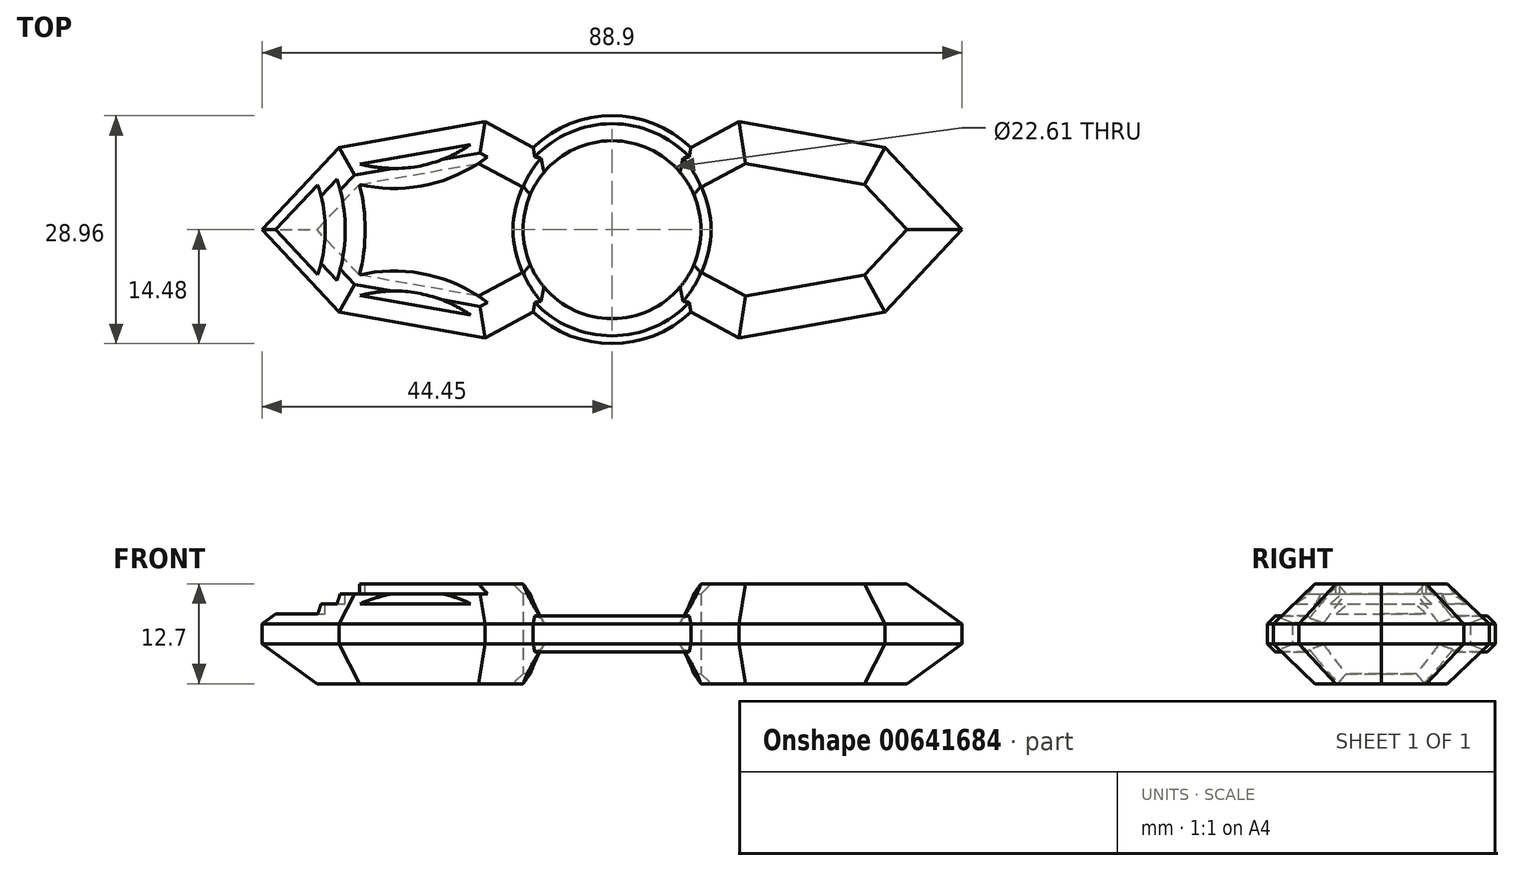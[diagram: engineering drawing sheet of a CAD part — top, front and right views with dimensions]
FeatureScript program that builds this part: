
annotation { "Feature Type Name" : "Feature", "Feature Type Description" : "" }
export const myFeature = defineFeature(function(context is Context, id is Id, definition is map)
    precondition{}
    {
        {
            var Q0;
            Q0=qCreatedBy(makeId("Top.planeOp"),FACE);
            var sketch = newSketch(context, id + "F0", { "sketchPlane" : qUnion([Q0])});
            skCircle(sketch, "E0", {"center": v(0, 0) * mm, "radius": 11.3 * mm});
            skArc(sketch, "E1", {"start": v(-10, -10.47) * mm, "mid": v(0, -14.48) * mm, "end": v(10, -10.47) * mm});
            skLineSegment(sketch, "E2", {"start": v(-10, 10.47) * mm, "end": v(-16.15, 13.73) * mm});
            skLineSegment(sketch, "E3", {"start": v(-34.65, 10.47) * mm, "end": v(-16.15, 13.73) * mm});
            skLineSegment(sketch, "E4", {"start": v(-44.45, 0) * mm, "end": v(-34.65, 10.47) * mm});
            skLineSegment(sketch, "E5", {"start": v(-44.45, 0) * mm, "end": v(44.45, 0) * mm, "construction": true});
            skLineSegment(sketch, "E6", {"start": v(0, 64.66) * mm, "end": v(0, -71.54) * mm, "construction": true});
            skArc(sketch, "E7.trimOffspring", {"start": v(10, 10.47) * mm, "mid": v(0, 14.48) * mm, "end": v(-10, 10.47) * mm});
            skLineSegment(sketch, "E8.MirrorCS", {"start": v(-44.45, 0) * mm, "end": v(-34.65, -10.47) * mm});
            skLineSegment(sketch, "E9.MirrorCS", {"start": v(-34.65, -10.47) * mm, "end": v(-16.15, -13.73) * mm});
            skLineSegment(sketch, "E10.MirrorCS", {"start": v(-10, -10.47) * mm, "end": v(-16.15, -13.73) * mm});
            skLineSegment(sketch, "E11.MirrorCS", {"start": v(10, 10.47) * mm, "end": v(16.15, 13.73) * mm});
            skLineSegment(sketch, "E12.MirrorCS", {"start": v(34.65, 10.47) * mm, "end": v(16.15, 13.73) * mm});
            skLineSegment(sketch, "E13.MirrorCS", {"start": v(44.45, 0) * mm, "end": v(34.65, 10.47) * mm});
            skLineSegment(sketch, "E14.MirrorCS", {"start": v(44.45, 0) * mm, "end": v(34.65, -10.47) * mm});
            skLineSegment(sketch, "E15.MirrorCS", {"start": v(34.65, -10.47) * mm, "end": v(16.15, -13.73) * mm});
            skLineSegment(sketch, "E16.MirrorCS", {"start": v(10, -10.47) * mm, "end": v(16.15, -13.73) * mm});
            skSolve(sketch);
        }
        {
            var Q0;
            Q0 = qSketchRegion(id + "F0", true);
            extrude(context, id + "F1", {"entities" : qUnion([Q0]), "endBound" : BoundingType.SYMMETRIC, "depth" : 12.7 * mm, "offsetDistance" : 25.4 * mm});
        }
        {
            var Q0;
            Q0=makeQuery(id+"F1.opExtrude","CAP_EDGE",EDGE,{"disambiguationData":[OSD([sQuery(id+"F0.wireOp",EDGE,"E8.MirrorCS")])],"isStart":false});
            var Q1;
            Q1=makeQuery(id+"F1.opExtrude","CAP_EDGE",EDGE,{"disambiguationData":[OSD([sQuery(id+"F0.wireOp",EDGE,"E4")])],"isStart":false});
            var Q2;
            Q2=makeQuery(id+"F1.opExtrude","CAP_EDGE",EDGE,{"disambiguationData":[OSD([sQuery(id+"F0.wireOp",EDGE,"E3")])],"isStart":false});
            var Q3;
            Q3=makeQuery(id+"F1.opExtrude","CAP_EDGE",EDGE,{"disambiguationData":[OSD([sQuery(id+"F0.wireOp",EDGE,"E2")])],"isStart":false});
            var Q4;
            Q4=makeQuery(id+"F1.opExtrude","CAP_EDGE",EDGE,{"disambiguationData":[OSD([sQuery(id+"F0.wireOp",EDGE,"E7.trimOffspring")])],"isStart":false});
            var Q5;
            Q5=makeQuery(id+"F1.opExtrude","CAP_EDGE",EDGE,{"disambiguationData":[OSD([sQuery(id+"F0.wireOp",EDGE,"E1")])],"isStart":false});
            var Q6;
            Q6=makeQuery(id+"F1.opExtrude","CAP_EDGE",EDGE,{"disambiguationData":[OSD([sQuery(id+"F0.wireOp",EDGE,"E10.MirrorCS")])],"isStart":false});
            var Q7;
            Q7=makeQuery(id+"F1.opExtrude","CAP_EDGE",EDGE,{"disambiguationData":[OSD([sQuery(id+"F0.wireOp",EDGE,"E9.MirrorCS")])],"isStart":false});
            var Q8;
            Q8=makeQuery(id+"F1.opExtrude","CAP_EDGE",EDGE,{"disambiguationData":[OSD([sQuery(id+"F0.wireOp",EDGE,"E15.MirrorCS")])],"isStart":false});
            var Q9;
            Q9=makeQuery(id+"F1.opExtrude","CAP_EDGE",EDGE,{"disambiguationData":[OSD([sQuery(id+"F0.wireOp",EDGE,"E16.MirrorCS")])],"isStart":false});
            var Q10;
            Q10=makeQuery(id+"F1.opExtrude","CAP_EDGE",EDGE,{"disambiguationData":[OSD([sQuery(id+"F0.wireOp",EDGE,"E14.MirrorCS")])],"isStart":false});
            var Q11;
            Q11=makeQuery(id+"F1.opExtrude","CAP_EDGE",EDGE,{"disambiguationData":[OSD([sQuery(id+"F0.wireOp",EDGE,"E13.MirrorCS")])],"isStart":false});
            var Q12;
            Q12=makeQuery(id+"F1.opExtrude","CAP_EDGE",EDGE,{"disambiguationData":[OSD([sQuery(id+"F0.wireOp",EDGE,"E12.MirrorCS")])],"isStart":false});
            var Q13;
            Q13=makeQuery(id+"F1.opExtrude","CAP_EDGE",EDGE,{"disambiguationData":[OSD([sQuery(id+"F0.wireOp",EDGE,"E11.MirrorCS")])],"isStart":false});
            var Q14;
            Q14=makeQuery(id+"F1.opExtrude","CAP_EDGE",EDGE,{"disambiguationData":[OSD([sQuery(id+"F0.wireOp",EDGE,"E15.MirrorCS")])],"isStart":true});
            var Q15;
            Q15=makeQuery(id+"F1.opExtrude","CAP_EDGE",EDGE,{"disambiguationData":[OSD([sQuery(id+"F0.wireOp",EDGE,"E14.MirrorCS")])],"isStart":true});
            var Q16;
            Q16=makeQuery(id+"F1.opExtrude","CAP_EDGE",EDGE,{"disambiguationData":[OSD([sQuery(id+"F0.wireOp",EDGE,"E13.MirrorCS")])],"isStart":true});
            var Q17;
            Q17=makeQuery(id+"F1.opExtrude","CAP_EDGE",EDGE,{"disambiguationData":[OSD([sQuery(id+"F0.wireOp",EDGE,"E12.MirrorCS")])],"isStart":true});
            var Q18;
            Q18=makeQuery(id+"F1.opExtrude","CAP_EDGE",EDGE,{"disambiguationData":[OSD([sQuery(id+"F0.wireOp",EDGE,"E11.MirrorCS")])],"isStart":true});
            var Q19;
            Q19=makeQuery(id+"F1.opExtrude","CAP_EDGE",EDGE,{"disambiguationData":[OSD([sQuery(id+"F0.wireOp",EDGE,"E7.trimOffspring")])],"isStart":true});
            var Q20;
            Q20=makeQuery(id+"F1.opExtrude","CAP_EDGE",EDGE,{"disambiguationData":[OSD([sQuery(id+"F0.wireOp",EDGE,"E2")])],"isStart":true});
            var Q21;
            Q21=makeQuery(id+"F1.opExtrude","CAP_EDGE",EDGE,{"disambiguationData":[OSD([sQuery(id+"F0.wireOp",EDGE,"E3")])],"isStart":true});
            var Q22;
            Q22=makeQuery(id+"F1.opExtrude","CAP_EDGE",EDGE,{"disambiguationData":[OSD([sQuery(id+"F0.wireOp",EDGE,"E4")])],"isStart":true});
            var Q23;
            Q23=makeQuery(id+"F1.opExtrude","CAP_EDGE",EDGE,{"disambiguationData":[OSD([sQuery(id+"F0.wireOp",EDGE,"E8.MirrorCS")])],"isStart":true});
            var Q24;
            Q24=makeQuery(id+"F1.opExtrude","CAP_EDGE",EDGE,{"disambiguationData":[OSD([sQuery(id+"F0.wireOp",EDGE,"E9.MirrorCS")])],"isStart":true});
            var Q25;
            Q25=makeQuery(id+"F1.opExtrude","CAP_EDGE",EDGE,{"disambiguationData":[OSD([sQuery(id+"F0.wireOp",EDGE,"E10.MirrorCS")])],"isStart":true});
            var Q26;
            Q26=makeQuery(id+"F1.opExtrude","CAP_EDGE",EDGE,{"disambiguationData":[OSD([sQuery(id+"F0.wireOp",EDGE,"E1")])],"isStart":true});
            var Q27;
            Q27=makeQuery(id+"F1.opExtrude","CAP_EDGE",EDGE,{"disambiguationData":[OSD([sQuery(id+"F0.wireOp",EDGE,"E16.MirrorCS")])],"isStart":true});
            chamfer(context, id + "F2", {"entities" : qUnion([Q0, Q1, Q2, Q3, Q4, Q5, Q6, Q7, Q8, Q9, Q10, Q11, Q12, Q13, Q14, Q15, Q16, Q17, Q18, Q19, Q20, Q21, Q22, Q23, Q24, Q25, Q26, Q27]), "width" : 5.08 * mm, "tangentPropagation" : true});
        }
        {
            var Q0;
            Q0=makeQuery(id+"F2.opChamfer","SPLIT",FACE,{"disambiguationData":[OD(0.0)],"derivedFrom":makeQuery(id+"F1.opExtrude","CAP_FACE",FACE,{"disambiguationData":[OSD([sQuery(id+"F0.wireOp",EDGE,"E0"),sQuery(id+"F0.wireOp",EDGE,"E1"),sQuery(id+"F0.wireOp",EDGE,"E2"),sQuery(id+"F0.wireOp",EDGE,"E3"),sQuery(id+"F0.wireOp",EDGE,"E4"),sQuery(id+"F0.wireOp",EDGE,"E7.trimOffspring"),sQuery(id+"F0.wireOp",EDGE,"E8.MirrorCS"),sQuery(id+"F0.wireOp",EDGE,"E9.MirrorCS"),sQuery(id+"F0.wireOp",EDGE,"E10.MirrorCS"),sQuery(id+"F0.wireOp",EDGE,"E11.MirrorCS"),sQuery(id+"F0.wireOp",EDGE,"E12.MirrorCS"),sQuery(id+"F0.wireOp",EDGE,"E13.MirrorCS"),sQuery(id+"F0.wireOp",EDGE,"E14.MirrorCS"),sQuery(id+"F0.wireOp",EDGE,"E15.MirrorCS"),sQuery(id+"F0.wireOp",EDGE,"E16.MirrorCS")])],"isStart":false})});
            var sketch = newSketch(context, id + "F3", { "sketchPlane" : qUnion([Q0])});
            skArc(sketch, "E17", {"start": v(-32.1, -5.76) * mm, "mid": v(-31.35, 0) * mm, "end": v(-32.1, 5.76) * mm});
            skArc(sketch, "E18", {"start": v(-46.92, -21.53) * mm, "mid": v(-13.43, -38.15) * mm, "end": v(-32.1, -5.76) * mm});
            skLineSegment(sketch, "E19", {"start": v(0, 0) * mm, "end": v(-114.26, 0) * mm, "construction": true});
            skLineSegment(sketch, "E20", {"start": v(-114.26, 0) * mm, "end": v(-130.65, 83.48) * mm, "construction": true});
            skArc(sketch, "E21.MirrorCS", {"start": v(-46.92, 21.53) * mm, "mid": v(-13.43, 38.15) * mm, "end": v(-32.1, 5.76) * mm});
            skArc(sketch, "E22.trimOffspring", {"start": v(-46.92, 21.53) * mm, "mid": v(-76.71, 0) * mm, "end": v(-46.92, -21.53) * mm});
            skSolve(sketch);
        }
        {
            var Q0;
            Q0 = qSketchRegion(id + "F3", true);
            extrude(context, id + "F4", {"entities" : qUnion([Q0]), "operationType" : NewBodyOperationType.REMOVE, "oppositeDirection" : true, "depth" : 1.27 * mm, "offsetDistance" : 25.4 * mm});
        }
        {
            var Q0;
            Q0=makeQuery(id+"F4.boolean.opBoolean","COPY",FACE,{"derivedFrom":makeQuery(id+"F4.opExtrude","CAP_FACE",FACE,{"disambiguationData":[OSD([sQuery(id+"F3.wireOp",EDGE,"E17")])],"isStart":false})});
            var sketch = newSketch(context, id + "F5", { "sketchPlane" : qUnion([Q0])});
            skArc(sketch, "E23.0", {"start": v(-42.5, 16.51) * mm, "mid": v(-15.28, 36.41) * mm, "end": v(-36.83, 10.48) * mm});
            skArc(sketch, "E23.1", {"start": v(-42.5, 16.51) * mm, "mid": v(-74.17, 0) * mm, "end": v(-42.5, -16.51) * mm});
            skArc(sketch, "E23.2", {"start": v(-42.5, -16.51) * mm, "mid": v(-15.28, -36.41) * mm, "end": v(-36.83, -10.48) * mm});
            skArc(sketch, "E23.3", {"start": v(-36.83, -10.48) * mm, "mid": v(-33.9, 0) * mm, "end": v(-36.83, 10.48) * mm});
            skSolve(sketch);
        }
        {
            var Q0;
            Q0 = qSketchRegion(id + "F5", true);
            extrude(context, id + "F6", {"entities" : qUnion([Q0]), "operationType" : NewBodyOperationType.REMOVE, "oppositeDirection" : true, "depth" : 1.27 * mm, "offsetDistance" : 25.4 * mm});
        }
        {
            var Q0;
            {var subQ2=sQuery(id+"F5.wireOp",EDGE,"E23.3");Q0=makeQuery(id+"F6.boolean.opBoolean","COPY",FACE,{"disambiguationData":[TD([makeQuery(id+"F6.opExtrude","SWEPT_FACE",FACE,{"disambiguationData":[OSD([subQ2])]})])],"derivedFrom":makeQuery(id+"F6.opExtrude","CAP_FACE",FACE,{"disambiguationData":[OSD([sQuery(id+"F5.wireOp",EDGE,"E23.0"),sQuery(id+"F5.wireOp",EDGE,"E23.1"),sQuery(id+"F5.wireOp",EDGE,"E23.2"),subQ2])],"isStart":false})});}
            var sketch = newSketch(context, id + "F7", { "sketchPlane" : qUnion([Q0])});
            skCircle(sketch, "E24", {"center": v(-54.03, 0) * mm, "radius": 17.6 * mm});
            skSolve(sketch);
        }
        {
            var Q0;
            Q0 = qSketchRegion(id + "F7", true);
            extrude(context, id + "F8", {"entities" : qUnion([Q0]), "operationType" : NewBodyOperationType.REMOVE, "oppositeDirection" : true, "depth" : 1.27 * mm, "offsetDistance" : 25.4 * mm});
        }
        {
            var Q0;
            Q0=makeQuery(id+"F1.opExtrude","SWEPT_FACE",FACE,{"disambiguationData":[OSD([sQuery(id+"F0.wireOp",EDGE,"E0")])]});
            chamfer(context, id + "F9", {"entities" : qUnion([Q0]), "width" : 1.27 * mm, "tangentPropagation" : true});
        }
    });
